# Revit family: Sanitary_Taps&Mixers_Zurn_Z842X1-XL_Wall-Mounted
name_source: partatom
category: Plumbing Fixtures
units: mm (PartAtom-declared; Revit-internal decimal feet)

## family parameters
Cut with Voids When Loaded = No
Host = Face
Maintain Annotation Orientation = No
OmniClass Number = 23.45.55.17
OmniClass Title = Mixing Faucets
Part Type = Normal
Room Calculation Point = No
Round Connector Dimension = Use Radius
Shared = No

## types (1)
- Z842X1-XL (PRE-RINSE FAUCET)
    Assembly Code = D2010.60
    CW Connection = Yes
    CWFU = 1
    Cold Water Connection Size (in) = 1/2"
    Default Elevation = 34"
    Description = Pre-Rinse Faucet
    Flow = 2 GPM
    HW Connection = Yes
    HWFU = 1
    Hot Water Connection Size (in) = 1/2"
    Main Material = Chrome-Plated Brass - Zurn - Polished
    Manufacturer = Zurn Industries, LLC
    Manufacturer Brand = Zurn
    Model = Z842X1-XL
    Modified date = 08/13/2025
    Product Documentation Link = https://www.zurn.com
    Product Page URL = https://www.zurn.com
    Product data url = https://bimobject.com
    URL = http://www.zurn.com
    Vent Connection = No
    WFU = 0
    Waste Connection = No

## geometry (parser evidence)
native form markers: Blend x4, Sweep x4
no freeform markers — native parametric forms only
